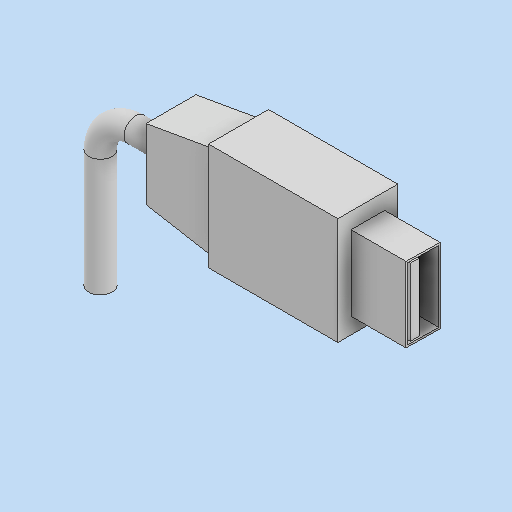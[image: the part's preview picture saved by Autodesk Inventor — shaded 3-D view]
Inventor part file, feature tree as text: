
AUTODESK INVENTOR PART (.ipt)
format: ipt  version: 2022 (Build 260153070, 153G)  size: 180,224 bytes
history: native  units: mm
features: extrude x4, other x3, plane x3, sketch x3, sweep x1, draft x1
ambient origin geometry x8: Origin, YZ Plane, XZ Plane, XY Plane, X Axis, Y Axis, Z Axis, Center Point
bodies: Solid1 (feature_tree), Solid2 (feature_tree)
feature tree (15):
  other  "P00173-09-002.ipt"
  plane  "Work Plane1"
  sketch  "Sketch3"  dims[d0=10.0mm d1=18.25mm d2=0.0mm]
  plane  "Work Plane2"
  plane  "Work Plane3"
  sketch  "Sketch5"  dims[d7=6.0mm d8=6.0mm d9=20.0mm d10=4.0mm d11=0.0mm d12=0.0mm d13=1.745329mm d14=0.7mm d15=0.5mm d16=0.2mm d17=1.5mm d18=12.5mm d19=7.5mm d20=0.0mm]
  sweep  "Sweep1"
  extrude  "Extrusion1"  Depth=12.75mm TaperAngle=0.0deg
  extrude  "Extrusion2"  Depth=6.0mm
  extrude  "Extrusion3"  Depth=1.5mm
  draft  "FaceDraft1"
  extrude  "Extrusion4"  Depth=1.5mm
  other  "USB_Position"
  other  "USB_Side"
  sketch  "Sketch4"  dims[d3=12.75mm d4=0.0mm d5=16.0mm d6=0.0mm]
